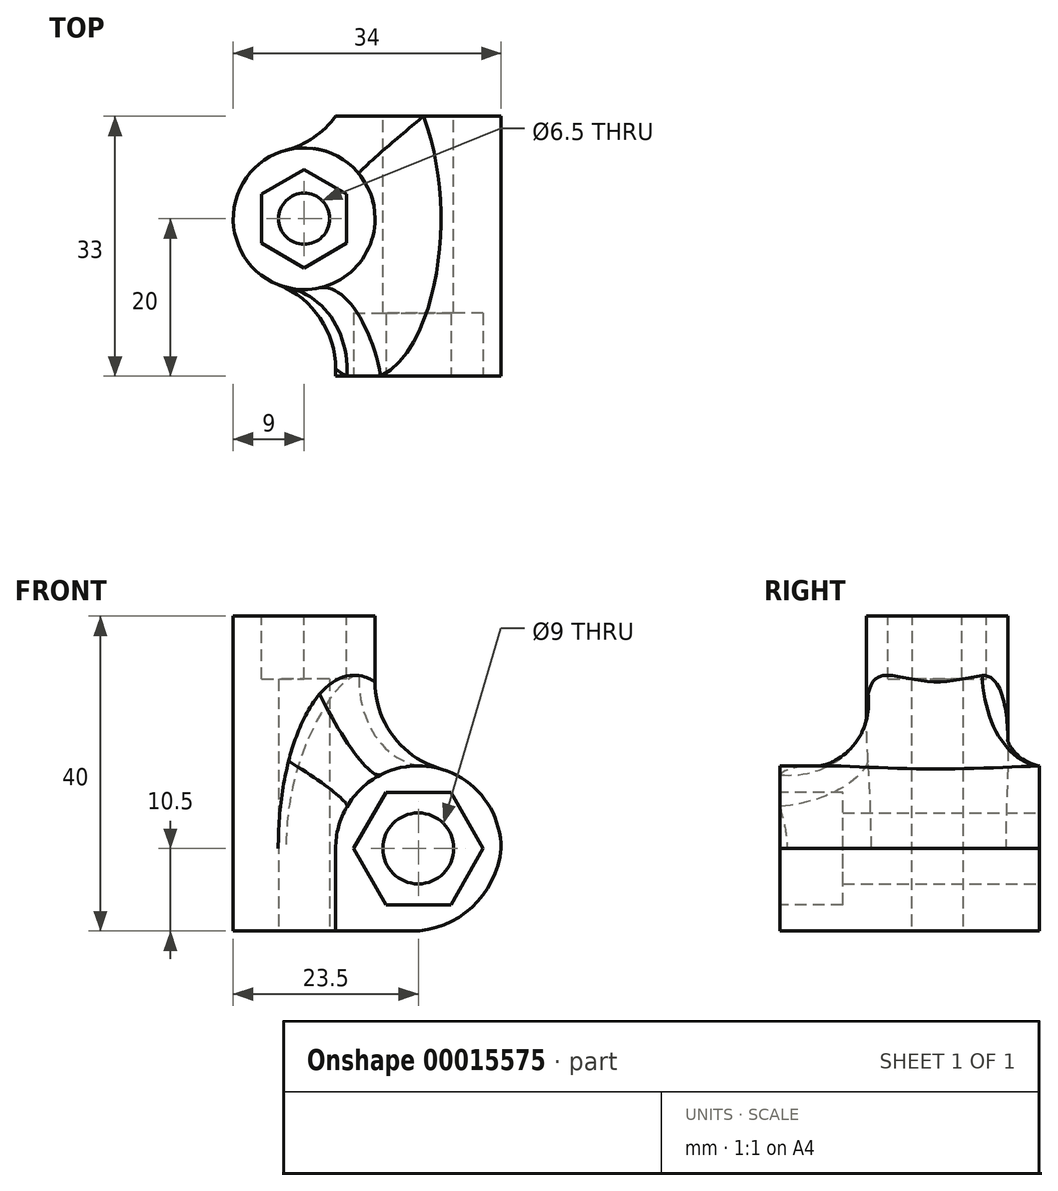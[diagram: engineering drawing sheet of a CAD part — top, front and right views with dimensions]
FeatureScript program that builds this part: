
annotation { "Feature Type Name" : "Feature", "Feature Type Description" : "" }
export const myFeature = defineFeature(function(context is Context, id is Id, definition is map)
    precondition{}
    {
        {
            var Q0;
            Q0=qCreatedBy(makeId("Top.planeOp"),FACE);
            var sketch = newSketch(context, id + "F0", { "sketchPlane" : qUnion([Q0])});
            skCircle(sketch, "E0", {"center": v(-7.5, 0) * mm, "radius": 3.25 * mm});
            skCircle(sketch, "E1.cCircle", {"center": v(-7.5, 0) * mm, "radius": 6.25 * mm, "construction": true});
            skLineSegment(sketch, "E1.0", {"start": v(-2.09, -3.13) * mm, "end": v(-7.5, -6.25) * mm});
            skLineSegment(sketch, "E1.1", {"start": v(-7.5, -6.25) * mm, "end": v(-12.91, -3.13) * mm});
            skLineSegment(sketch, "E1.2", {"start": v(-12.91, -3.13) * mm, "end": v(-12.91, 3.12) * mm});
            skLineSegment(sketch, "E1.3", {"start": v(-12.91, 3.12) * mm, "end": v(-7.5, 6.25) * mm});
            skLineSegment(sketch, "E1.4", {"start": v(-7.5, 6.25) * mm, "end": v(-2.09, 3.13) * mm});
            skLineSegment(sketch, "E1.5", {"start": v(-2.09, 3.13) * mm, "end": v(-2.09, -3.13) * mm});
            skCircle(sketch, "E2", {"center": v(-7.5, 0) * mm, "radius": 9 * mm});
            skSolve(sketch);
        }
        {
            var Q0;
            Q0=qCreatedBy(makeId("Top.planeOp"),FACE);
            var sketch = newSketch(context, id + "F1", { "sketchPlane" : qUnion([Q0])});
            skCircle(sketch, "E3.0", {"center": v(-7.5, 0) * mm, "radius": 9 * mm});
            skCircle(sketch, "E3.1", {"center": v(-7.5, 0) * mm, "radius": 3.25 * mm});
            skSolve(sketch);
        }
        {
            var Q0;
            Q0 = qSketchRegion(id + "F1", true);
            extrude(context, id + "F2", {"entities" : qUnion([Q0]), "depth" : 40 * mm});
        }
        {
            var Q0;
            Q0=makeQuery(id+"F2.opExtrude","CAP_FACE",FACE,{"disambiguationData":[OSD([sQuery(id+"F1.wireOp",EDGE,"E3.0"),sQuery(id+"F1.wireOp",EDGE,"E3.1")])],"isStart":false});
            var sketch = newSketch(context, id + "F3", { "sketchPlane" : qUnion([Q0])});
            skLineSegment(sketch, "E4.0", {"start": v(-12.91, 3.12) * mm, "end": v(-7.5, 6.25) * mm});
            skLineSegment(sketch, "E4.1", {"start": v(-7.5, 6.25) * mm, "end": v(-2.09, 3.13) * mm});
            skLineSegment(sketch, "E4.2", {"start": v(-2.09, 3.13) * mm, "end": v(-2.09, -3.13) * mm});
            skLineSegment(sketch, "E4.3", {"start": v(-2.09, -3.13) * mm, "end": v(-7.5, -6.25) * mm});
            skLineSegment(sketch, "E4.4", {"start": v(-7.5, -6.25) * mm, "end": v(-12.91, -3.13) * mm});
            skLineSegment(sketch, "E4.5", {"start": v(-12.91, -3.13) * mm, "end": v(-12.91, 3.12) * mm});
            skSolve(sketch);
        }
        {
            var Q0;
            Q0 = qSketchRegion(id + "F3", true);
            extrude(context, id + "F4", {"entities" : qUnion([Q0]), "operationType" : NewBodyOperationType.REMOVE, "oppositeDirection" : true, "depth" : 8 * mm});
        }
        {
            var Q0;
            Q0=qCreatedBy(makeId("Front.planeOp"),FACE);
            var sketch = newSketch(context, id + "F5", { "sketchPlane" : qUnion([Q0])});
            skLineSegment(sketch, "E5.bottom", {"start": v(-3.5, 21) * mm, "end": v(17.5, 21) * mm});
            skLineSegment(sketch, "E5.top", {"start": v(-3.5, 0) * mm, "end": v(17.5, 0) * mm});
            skLineSegment(sketch, "E5.left", {"start": v(-3.5, 21) * mm, "end": v(-3.5, 0) * mm});
            skLineSegment(sketch, "E5.right", {"start": v(17.5, 21) * mm, "end": v(17.5, 0) * mm});
            skCircle(sketch, "E6", {"center": v(7, 10.5) * mm, "radius": 10.5 * mm});
            skCircle(sketch, "E7.cCircle", {"center": v(7, 10.5) * mm, "radius": 8.25 * mm, "construction": true});
            skLineSegment(sketch, "E7.0", {"start": v(11.12, 3.36) * mm, "end": v(2.88, 3.36) * mm});
            skLineSegment(sketch, "E7.1", {"start": v(2.88, 3.36) * mm, "end": v(-1.25, 10.5) * mm});
            skLineSegment(sketch, "E7.2", {"start": v(-1.25, 10.5) * mm, "end": v(2.88, 17.64) * mm});
            skLineSegment(sketch, "E7.3", {"start": v(2.88, 17.64) * mm, "end": v(11.12, 17.64) * mm});
            skLineSegment(sketch, "E7.4", {"start": v(11.12, 17.64) * mm, "end": v(15.25, 10.5) * mm});
            skLineSegment(sketch, "E7.5", {"start": v(15.25, 10.5) * mm, "end": v(11.12, 3.36) * mm});
            skCircle(sketch, "E8", {"center": v(7, 10.5) * mm, "radius": 4.5 * mm});
            skSolve(sketch);
        }
        {
            var Q0;
            Q0=qCreatedBy(makeId("Front.planeOp"),FACE);
            var sketch = newSketch(context, id + "F6", { "sketchPlane" : qUnion([Q0])});
            skLineSegment(sketch, "E9.0", {"start": v(-3.5, 10.5) * mm, "end": v(-3.5, 0) * mm});
            skLineSegment(sketch, "E9.2", {"start": v(17.5, 10.5) * mm, "end": v(17.5, 0) * mm});
            skArc(sketch, "E9.3", {"start": v(17.5, 10.5) * mm, "mid": v(7, 21) * mm, "end": v(-3.5, 10.5) * mm});
            skLineSegment(sketch, "E9.4", {"start": v(-3.5, 0) * mm, "end": v(17.5, 0) * mm});
            skCircle(sketch, "E9.5", {"center": v(7, 10.5) * mm, "radius": 4.5 * mm});
            skPoint(sketch, "E10.orphan", {"position": v(-3.5, 21) * mm});
            skPoint(sketch, "E9.1.end.orphan", {"position": v(17.5, 21) * mm});
            skSolve(sketch);
        }
        {
            var Q0;
            Q0 = qSketchRegion(id + "F6", true);
            extrude(context, id + "F7", {"entities" : qUnion([Q0]), "operationType" : NewBodyOperationType.ADD, "depth" : 20 * mm, "hasSecondDirection" : true, "secondDirectionOppositeDirection" : true, "secondDirectionDepth" : 13 * mm});
        }
        {
            var Q0;
            Q0=makeQuery(id+"F7.opExtrude","CAP_FACE",FACE,{"disambiguationData":[OSD([sQuery(id+"F6.wireOp",EDGE,"E9.0"),sQuery(id+"F6.wireOp",EDGE,"E9.2"),sQuery(id+"F6.wireOp",EDGE,"E9.3"),sQuery(id+"F6.wireOp",EDGE,"E9.4"),sQuery(id+"F6.wireOp",EDGE,"E9.5")])],"isStart":false});
            var sketch = newSketch(context, id + "F8", { "sketchPlane" : qUnion([Q0])});
            skLineSegment(sketch, "E11.0", {"start": v(2.88, 17.64) * mm, "end": v(11.12, 17.64) * mm});
            skLineSegment(sketch, "E11.1", {"start": v(-1.25, 10.5) * mm, "end": v(2.88, 17.64) * mm});
            skLineSegment(sketch, "E11.2", {"start": v(11.12, 17.64) * mm, "end": v(15.25, 10.5) * mm});
            skLineSegment(sketch, "E11.3", {"start": v(15.25, 10.5) * mm, "end": v(11.12, 3.36) * mm});
            skLineSegment(sketch, "E11.4", {"start": v(11.12, 3.36) * mm, "end": v(2.88, 3.36) * mm});
            skLineSegment(sketch, "E11.5", {"start": v(2.88, 3.36) * mm, "end": v(-1.25, 10.5) * mm});
            skSolve(sketch);
        }
        {
            var Q0;
            Q0 = qSketchRegion(id + "F8", true);
            extrude(context, id + "F9", {"entities" : qUnion([Q0]), "operationType" : NewBodyOperationType.REMOVE, "oppositeDirection" : true, "depth" : 8 * mm});
        }
        {
            var Q0;
            Q0=makeQuery(id+"F7.boolean.opBoolean","INTERSECT",EDGE,{"disambiguationData":[OD(0.0)],"derivedFrom":[makeQuery(id+"F2.opExtrude","SWEPT_FACE",FACE,{"disambiguationData":[OSD([sQuery(id+"F1.wireOp",EDGE,"E3.0")])]}),makeQuery(id+"F7.opExtrude","SWEPT_FACE",FACE,{"disambiguationData":[OSD([sQuery(id+"F6.wireOp",EDGE,"E9.0")])]})]});
            var Q1;
            Q1=makeQuery(id+"F7.opExtrude","SWEPT_EDGE",EDGE,{"disambiguationData":[OSD([sQuery(id+"F6.wireOp",EDGE,"E9.2"),sQuery(id+"F6.wireOp",EDGE,"E9.4")])]});
            fillet(context, id + "F10", {"entities" : qUnion([Q0, Q1]), "radius" : 11.5 * mm, "tangentPropagation" : true, "allowEdgeOverflow" : false});
        }
    });
